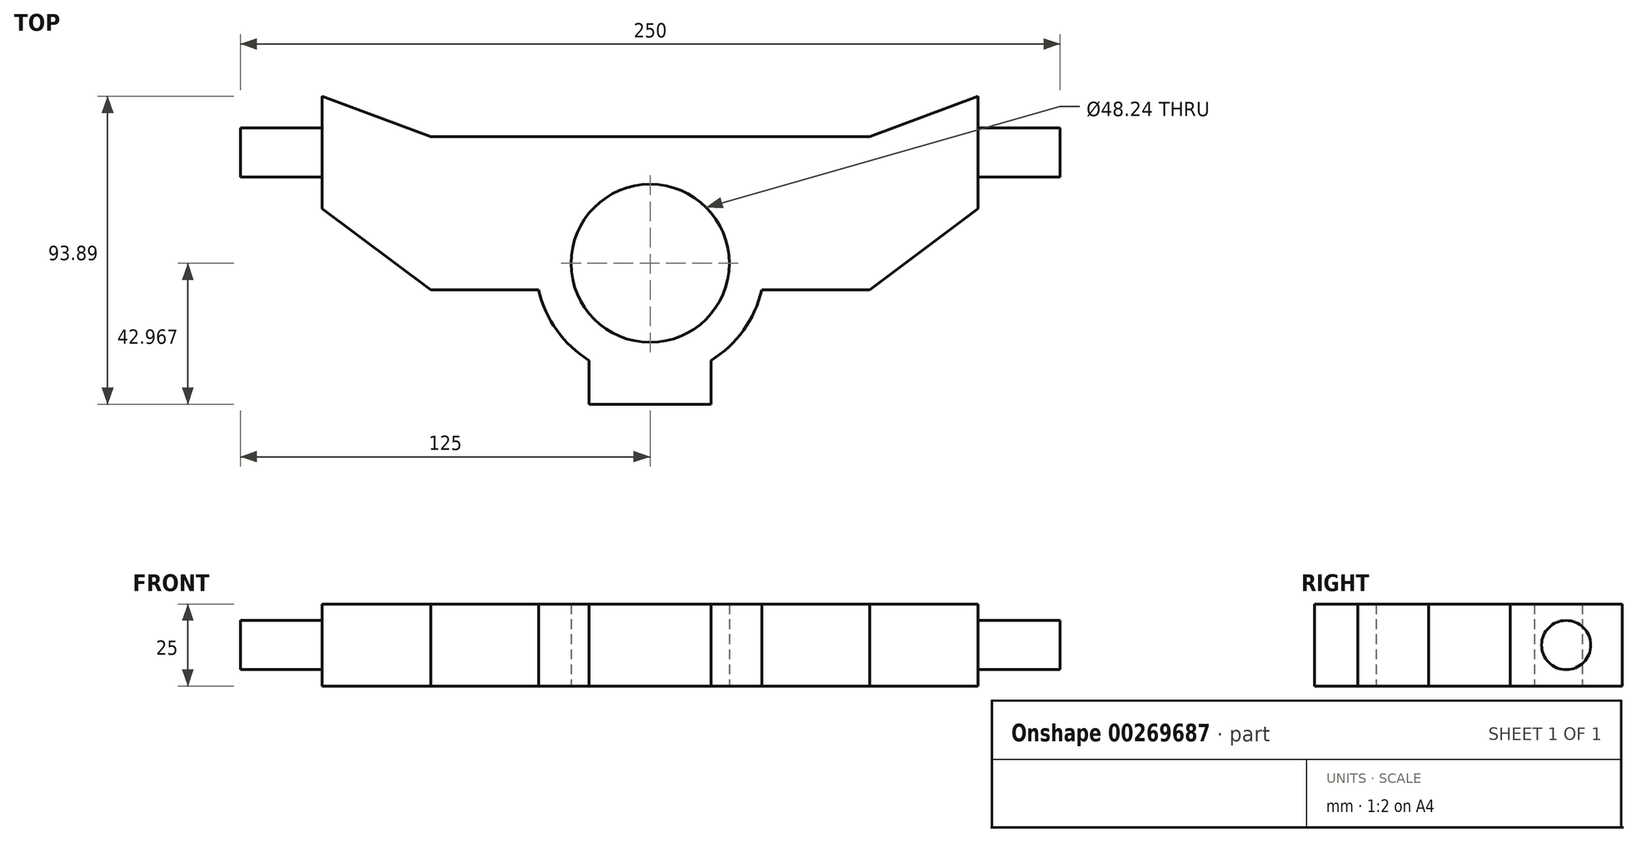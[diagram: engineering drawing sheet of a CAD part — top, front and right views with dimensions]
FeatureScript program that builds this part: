
annotation { "Feature Type Name" : "Feature", "Feature Type Description" : "" }
export const myFeature = defineFeature(function(context is Context, id is Id, definition is map)
    precondition{}
    {
        {
            var Q0;
            Q0=qCreatedBy(makeId("Top.planeOp"),FACE);
            var sketch = newSketch(context, id + "F0", { "sketchPlane" : qUnion([Q0])});
            skLineSegment(sketch, "E0", {"start": v(0, -64.44) * mm, "end": v(0, -45.6) * mm});
            skLineSegment(sketch, "E1", {"start": v(0, 17.18) * mm, "end": v(-66.9, 17.18) * mm});
            skLineSegment(sketch, "E2", {"start": v(-66.9, 17.18) * mm, "end": v(-100, 29.45) * mm});
            skLineSegment(sketch, "E3", {"start": v(-100, 29.45) * mm, "end": v(-100, -4.77) * mm});
            skLineSegment(sketch, "E4", {"start": v(-100, -4.77) * mm, "end": v(-66.9, -29.6) * mm});
            skLineSegment(sketch, "E5", {"start": v(-66.9, -29.6) * mm, "end": v(-34.05, -29.6) * mm});
            skArc(sketch, "E6", {"start": v(-18.58, -51.14) * mm, "mid": v(-28.44, -41.89) * mm, "end": v(-34.05, -29.6) * mm});
            skArc(sketch, "E7", {"start": v(0, -45.6) * mm, "mid": v(-24.12, -21.47) * mm, "end": v(0, 2.65) * mm});
            skLineSegment(sketch, "E8", {"start": v(0, -64.44) * mm, "end": v(-18.58, -64.44) * mm});
            skLineSegment(sketch, "E9", {"start": v(-18.58, -64.44) * mm, "end": v(-18.58, -51.14) * mm});
            skLineSegment(sketch, "E10.MirrorCS", {"start": v(18.58, -64.44) * mm, "end": v(18.58, -51.14) * mm});
            skLineSegment(sketch, "E11.MirrorCS", {"start": v(100, 29.45) * mm, "end": v(100, -4.77) * mm});
            skLineSegment(sketch, "E12.MirrorCS", {"start": v(66.9, 17.18) * mm, "end": v(100, 29.45) * mm});
            skArc(sketch, "E13.MirrorCS", {"start": v(18.58, -51.14) * mm, "mid": v(28.44, -41.89) * mm, "end": v(34.05, -29.6) * mm});
            skLineSegment(sketch, "E14.MirrorCS", {"start": v(100, -4.77) * mm, "end": v(66.9, -29.6) * mm});
            skLineSegment(sketch, "E15.MirrorCS", {"start": v(66.9, -29.6) * mm, "end": v(34.05, -29.6) * mm});
            skLineSegment(sketch, "E16.MirrorCS", {"start": v(0, 17.18) * mm, "end": v(66.9, 17.18) * mm});
            skArc(sketch, "E17.MirrorCS", {"start": v(0, -45.6) * mm, "mid": v(24.12, -21.47) * mm, "end": v(0, 2.65) * mm});
            skLineSegment(sketch, "E18.MirrorCS", {"start": v(0, -64.44) * mm, "end": v(18.58, -64.44) * mm});
            skSolve(sketch);
        }
        {
            var Q0;
            Q0 = qSketchRegion(id + "F0", true);
            extrude(context, id + "F1", {"entities" : qUnion([Q0]), "depth" : 25 * mm});
        }
        {
            var Q0;
            Q0=makeQuery(id+"F1.opExtrude","SWEPT_FACE",FACE,{"disambiguationData":[OSD([sQuery(id+"F0.wireOp",EDGE,"E3")])]});
            var sketch = newSketch(context, id + "F2", { "sketchPlane" : qUnion([Q0])});
            skLineSegment(sketch, "E19", {"start": v(-29.45, 0) * mm, "end": v(4.77, 25) * mm, "construction": true});
            skCircle(sketch, "E20", {"center": v(-12.34, 12.5) * mm, "radius": 7.5 * mm});
            skSolve(sketch);
        }
        {
            var Q0;
            Q0 = qSketchRegion(id + "F2", true);
            extrude(context, id + "F3", {"entities" : qUnion([Q0]), "depth" : 25 * mm});
        }
        {
            var Q0;
            Q0=makeQuery(id+"F3.opExtrude","SWEPT_BODY",BODY,{"disambiguationData":[OSD([sQuery(id+"F2.wireOp",EDGE,"E20")])]});
            var Q1;
            Q1=qCreatedBy(makeId("Right.planeOp"),FACE);
            mirror(context, id + "F4", {"operationType" : NewBodyOperationType.ADD, "entities" : qUnion([Q0]), "mirrorPlane" : qUnion([Q1])});
        }
    });
